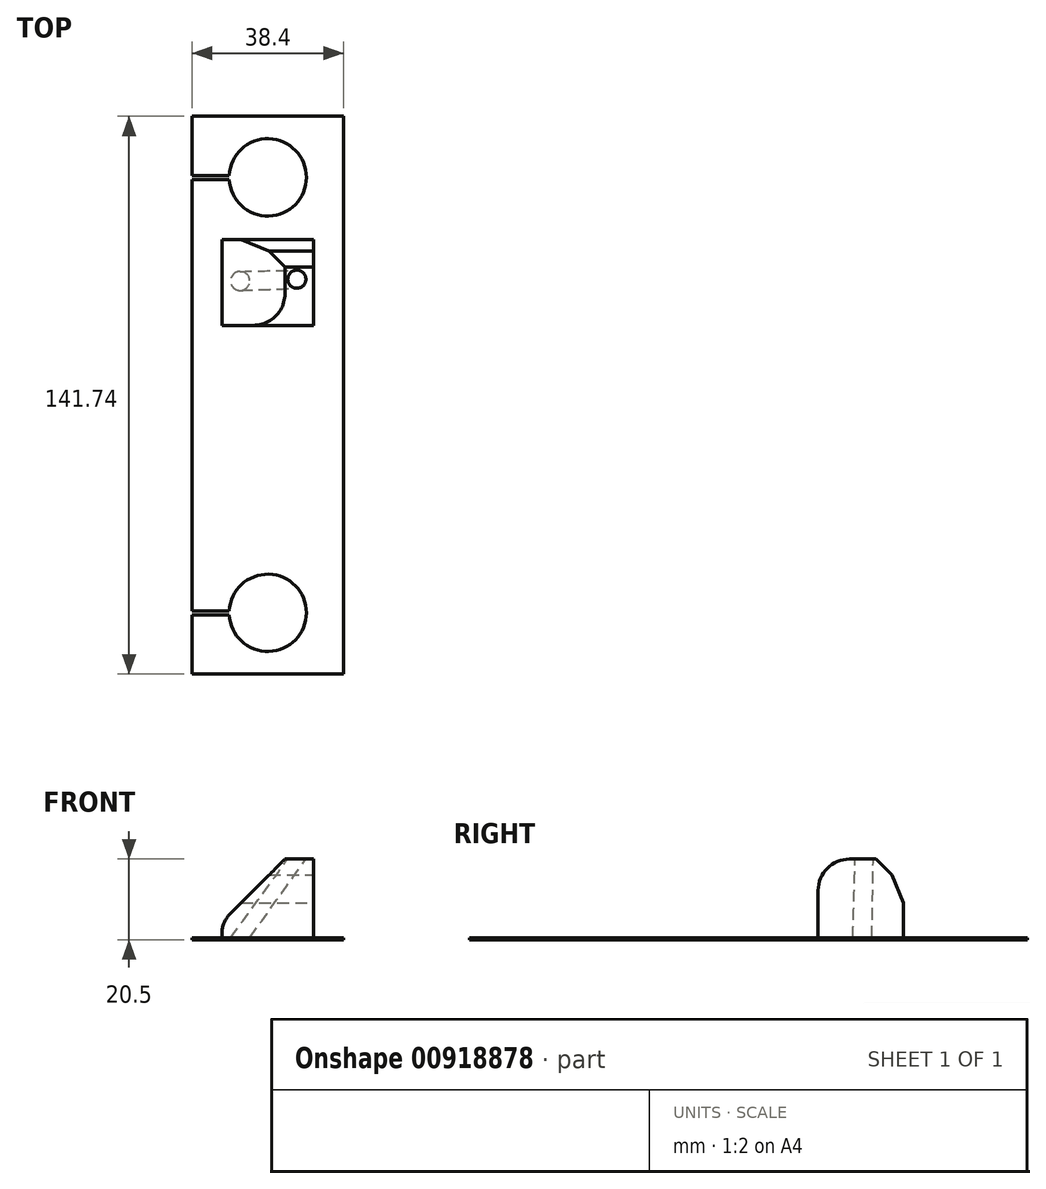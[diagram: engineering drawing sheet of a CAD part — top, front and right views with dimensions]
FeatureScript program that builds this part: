
annotation { "Feature Type Name" : "Feature", "Feature Type Description" : "" }
export const myFeature = defineFeature(function(context is Context, id is Id, definition is map)
    precondition{}
    {
        {
            var Q0;
            Q0=qCreatedBy(makeId("Top.planeOp"),FACE);
            var sketch = newSketch(context, id + "F0", { "sketchPlane" : qUnion([Q0])});
            skLineSegment(sketch, "E0.bottom", {"start": v(-19.2, 70.87) * mm, "end": v(19.2, 70.87) * mm});
            skLineSegment(sketch, "E0.top", {"start": v(-19.2, -70.87) * mm, "end": v(19.2, -70.87) * mm});
            skLineSegment(sketch, "E0.left", {"start": v(-19.2, 70.87) * mm, "end": v(-19.2, 55.82) * mm});
            skLineSegment(sketch, "E0.right", {"start": v(19.2, 70.87) * mm, "end": v(19.2, -70.87) * mm});
            skPoint(sketch, "E0.middle", {"position": v(0, 0) * mm});
            skArc(sketch, "E1", {"start": v(-9.8, 54.82) * mm, "mid": v(9.82, 55.32) * mm, "end": v(-9.8, 55.82) * mm});
            skLineSegment(sketch, "E2.bottom", {"start": v(-9.8, 54.82) * mm, "end": v(-19.2, 54.82) * mm});
            skLineSegment(sketch, "E2.top", {"start": v(-9.8, 55.82) * mm, "end": v(-19.2, 55.82) * mm});
            skLineSegment(sketch, "E3.trimOffspring", {"start": v(-19.2, 54.82) * mm, "end": v(-19.2, -54.82) * mm});
            skLineSegment(sketch, "E4", {"start": v(19.2, 0) * mm, "end": v(-19.2, 0) * mm, "construction": true});
            skArc(sketch, "E5.MirrorCS", {"start": v(-9.8, -54.82) * mm, "mid": v(9.82, -55.32) * mm, "end": v(-9.8, -55.82) * mm});
            skLineSegment(sketch, "E6.MirrorCS", {"start": v(-9.8, -54.82) * mm, "end": v(-19.2, -54.82) * mm});
            skLineSegment(sketch, "E7.MirrorCS", {"start": v(-9.8, -55.82) * mm, "end": v(-19.2, -55.82) * mm});
            skLineSegment(sketch, "E8.trimOffspring", {"start": v(-19.2, -55.82) * mm, "end": v(-19.2, -70.87) * mm});
            skSolve(sketch);
        }
        {
            var Q0;
            Q0=makeQuery(id+"F0.imprint","IMPRINT",FACE,{"disambiguationData":[TD([[makeQuery(id+"F0.imprint","IMPRINT",EDGE,{"derivedFrom":sQuery(id+"F0.wireOp",EDGE,"E0.bottom")}),-1.0]])]});
            extrude(context, id + "F1", {"entities" : qUnion([Q0]), "depth" : 0.5 * mm, "offsetDistance" : 25 * mm});
        }
        {
            var Q0;
            Q0=makeQuery(id+"F1.opExtrude","CAP_FACE",FACE,{"disambiguationData":[OSD([sQuery(id+"F0.wireOp",EDGE,"E0.bottom"),sQuery(id+"F0.wireOp",EDGE,"E0.top"),sQuery(id+"F0.wireOp",EDGE,"E0.left"),sQuery(id+"F0.wireOp",EDGE,"E0.right"),sQuery(id+"F0.wireOp",EDGE,"E1"),sQuery(id+"F0.wireOp",EDGE,"E2.bottom"),sQuery(id+"F0.wireOp",EDGE,"E2.top"),sQuery(id+"F0.wireOp",EDGE,"E3.trimOffspring"),sQuery(id+"F0.wireOp",EDGE,"E5.MirrorCS"),sQuery(id+"F0.wireOp",EDGE,"E6.MirrorCS"),sQuery(id+"F0.wireOp",EDGE,"E7.MirrorCS"),sQuery(id+"F0.wireOp",EDGE,"E8.trimOffspring")])],"isStart":false});
            var sketch = newSketch(context, id + "F2", { "sketchPlane" : qUnion([Q0])});
            skLineSegment(sketch, "E9.bottom", {"start": v(-11.64, 17.74) * mm, "end": v(11.64, 17.74) * mm});
            skLineSegment(sketch, "E9.top", {"start": v(-11.64, 39.47) * mm, "end": v(11.64, 39.47) * mm});
            skLineSegment(sketch, "E9.left", {"start": v(-11.64, 17.74) * mm, "end": v(-11.64, 39.47) * mm});
            skLineSegment(sketch, "E9.right", {"start": v(11.64, 17.74) * mm, "end": v(11.64, 39.47) * mm});
            skPoint(sketch, "E9.middle", {"position": v(0, 28.6) * mm});
            skSolve(sketch);
        }
        {
            var Q0;
            Q0 = qSketchRegion(id + "F2", true);
            extrude(context, id + "F3", {"entities" : qUnion([Q0]), "operationType" : NewBodyOperationType.ADD, "depth" : 20 * mm, "offsetDistance" : 25 * mm});
        }
        {
            var Q0;
            Q0=qCreatedBy(makeId("Top.planeOp"),FACE);
            cPlane(context, id + "F4", {"entities" : qUnion([Q0]), "cplaneType" : CPlaneType.OFFSET, "offset" : 0.5 * mm, "width" : 150 * mm, "height" : 150 * mm});
        }
        {
            var Q0;
            Q0=qCreatedBy(id+"F4.planeOp",FACE);
            var sketch = newSketch(context, id + "F5", { "sketchPlane" : qUnion([Q0])});
            skCircle(sketch, "E10", {"center": v(-7, 29) * mm, "radius": 2.42 * mm});
            skSolve(sketch);
        }
        {
            var Q0;
            Q0=makeQuery(id+"F3.opExtrude","CAP_FACE",FACE,{"disambiguationData":[OSD([sQuery(id+"F2.wireOp",EDGE,"E9.bottom"),sQuery(id+"F2.wireOp",EDGE,"E9.top"),sQuery(id+"F2.wireOp",EDGE,"E9.left"),sQuery(id+"F2.wireOp",EDGE,"E9.right")])],"isStart":false});
            var sketch = newSketch(context, id + "F6", { "sketchPlane" : qUnion([Q0])});
            skCircle(sketch, "E11", {"center": v(7.38, 29.45) * mm, "radius": 2.3 * mm});
            skSolve(sketch);
        }
        {
            var Q1;
            Q1 = qSketchRegion(id + "F6", true);
            var Q2;
            Q2 = qSketchRegion(id + "F5", true);
            loft(context, id + "F7", {"operationType" : NewBodyOperationType.REMOVE, "sheetProfilesArray" : [{ "sheetProfileEntities" : qUnion([Q1]) }, { "sheetProfileEntities" : qUnion([Q2]) }]});
        }
        {
            var Q0;
            Q0=makeQuery(id+"F3.opExtrude","CAP_EDGE",EDGE,{"disambiguationData":[OSD([sQuery(id+"F2.wireOp",EDGE,"E9.left")])],"isStart":false});
            chamfer(context, id + "F8", {"entities" : qUnion([Q0]), "width" : 16 * mm, "tangentPropagation" : true});
        }
        {
            var Q0;
            Q0=makeQuery(id+"F3.opExtrude","CAP_EDGE",EDGE,{"disambiguationData":[OSD([sQuery(id+"F2.wireOp",EDGE,"E9.bottom")])],"isStart":false});
            fillet(context, id + "F9", {"entities" : qUnion([Q0]), "radius" : 8 * mm, "tangentPropagation" : true, "allowEdgeOverflow" : false});
        }
        {
            var Q0;
            {var subQ0=sQuery(id+"F2.wireOp",EDGE,"E9.left");Q0=makeQuery(id+"F8.opChamfer","BLEND_EDGE",EDGE,{"blendedFrom":[makeQuery(id+"F3.opExtrude","CAP_EDGE",EDGE,{"disambiguationData":[OSD([subQ0])],"isStart":false}),makeQuery(id+"F3.opExtrude","SWEPT_FACE",FACE,{"disambiguationData":[OSD([subQ0])]})],"blendedInto":[makeQuery(id+"F3.opExtrude","SWEPT_FACE",FACE,{"disambiguationData":[OSD([subQ0])]})]});}
            fillet(context, id + "F10", {"entities" : qUnion([Q0]), "radius" : 7 * mm, "tangentPropagation" : true, "allowEdgeOverflow" : false});
        }
        {
            var Q0;
            Q0=makeQuery(id+"F3.opExtrude","CAP_EDGE",EDGE,{"disambiguationData":[OSD([sQuery(id+"F2.wireOp",EDGE,"E9.top")])],"isStart":false});
            chamfer(context, id + "F11", {"entities" : qUnion([Q0]), "width" : 7 * mm, "tangentPropagation" : true});
        }
        {
            var Q0;
            {var subQ0=sQuery(id+"F2.wireOp",EDGE,"E9.top");Q0=makeQuery(id+"F11.opChamfer","BLEND_EDGE",EDGE,{"blendedFrom":[makeQuery(id+"F3.opExtrude","CAP_EDGE",EDGE,{"disambiguationData":[OSD([subQ0])],"isStart":false}),makeQuery(id+"F3.opExtrude","SWEPT_FACE",FACE,{"disambiguationData":[OSD([subQ0])]})],"blendedInto":[makeQuery(id+"F3.opExtrude","SWEPT_FACE",FACE,{"disambiguationData":[OSD([subQ0])]})]});}
            chamfer(context, id + "F12", {"entities" : qUnion([Q0]), "width" : 10 * mm, "tangentPropagation" : true});
        }
    });
